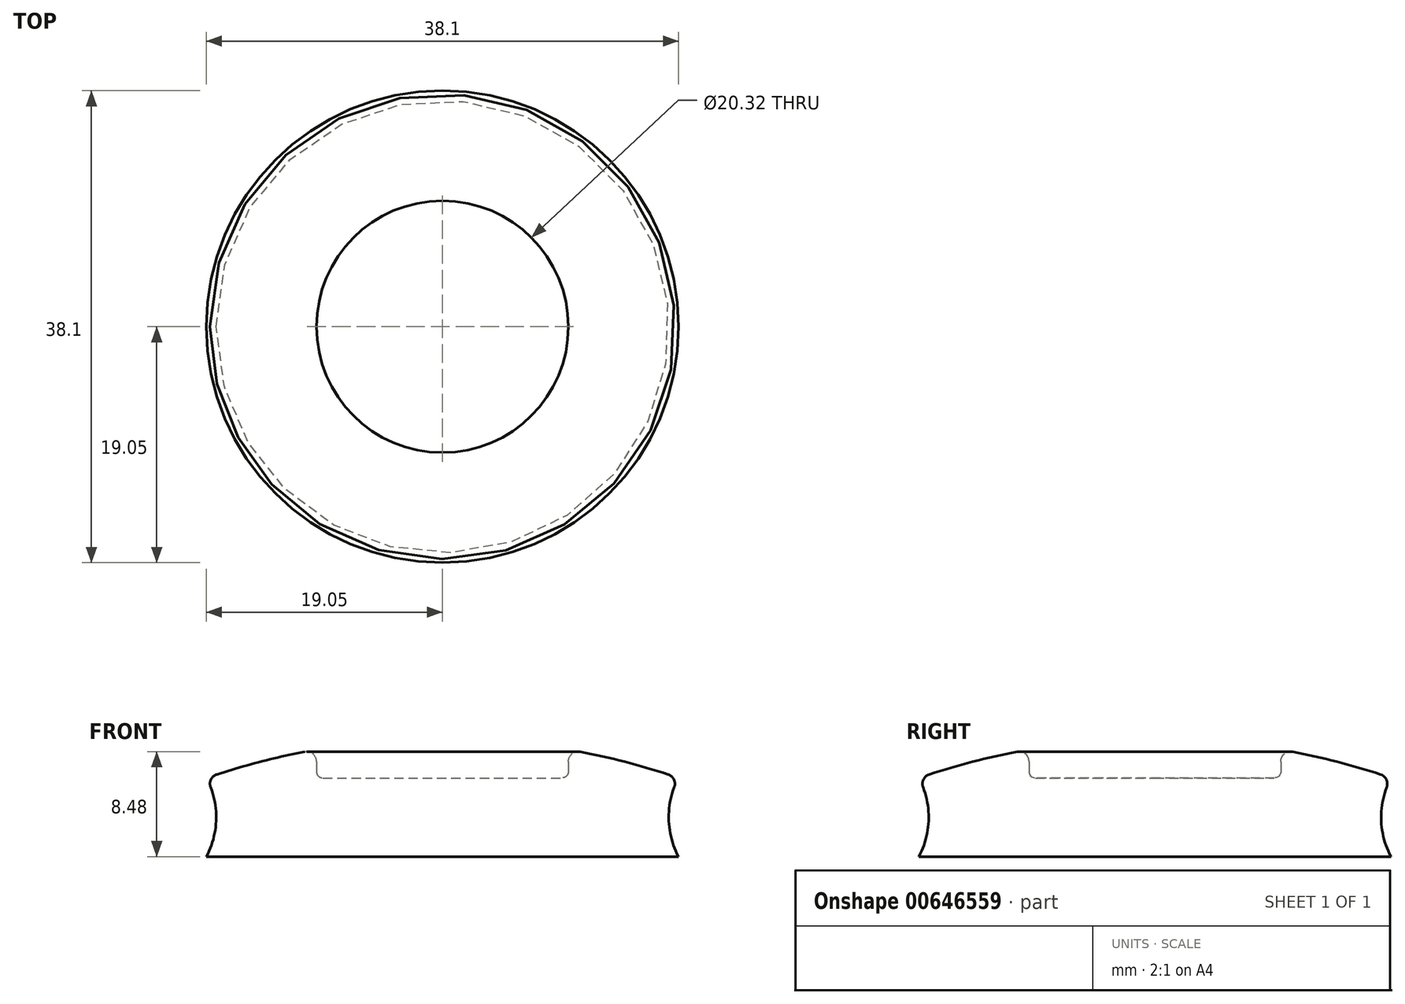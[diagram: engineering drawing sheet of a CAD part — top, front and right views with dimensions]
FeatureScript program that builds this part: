
annotation { "Feature Type Name" : "Feature", "Feature Type Description" : "" }
export const myFeature = defineFeature(function(context is Context, id is Id, definition is map)
    precondition{}
    {
        {
            var Q0;
            Q0=qCreatedBy(makeId("Front.planeOp"),FACE);
            var sketch = newSketch(context, id + "F0", { "sketchPlane" : qUnion([Q0])});
            skLineSegment(sketch, "E0.bottom", {"start": v(0, 0) * mm, "end": v(-19.05, 0) * mm});
            skLineSegment(sketch, "E0.top", {"start": v(0, 6.35) * mm, "end": v(-10.16, 6.35) * mm});
            skLineSegment(sketch, "E0.left", {"start": v(0, 0) * mm, "end": v(0, 6.35) * mm});
            skArc(sketch, "E1", {"start": v(-19.05, 0) * mm, "mid": v(-18.27, 2.76) * mm, "end": v(-18.7, 5.6) * mm});
            skLineSegment(sketch, "E2", {"start": v(0, 6.35) * mm, "end": v(19.05, 6.35) * mm});
            skLineSegment(sketch, "E3", {"start": v(0, 0) * mm, "end": v(19.05, 0) * mm});
            skArc(sketch, "E4", {"start": v(19.05, 6.35) * mm, "mid": v(14.65, 7.67) * mm, "end": v(10.16, 8.64) * mm});
            skLineSegment(sketch, "E5.bottom", {"start": v(-9.64, 6.35) * mm, "end": v(10.16, 6.35) * mm});
            skLineSegment(sketch, "E5.left", {"start": v(-10.16, 6.87) * mm, "end": v(-10.16, 7.67) * mm});
            skLineSegment(sketch, "E5.right", {"start": v(10.16, 6.35) * mm, "end": v(10.16, 8.64) * mm});
            skArc(sketch, "E6.trimOffspring", {"start": v(-11.12, 8.46) * mm, "mid": v(-14.7, 7.66) * mm, "end": v(-18.2, 6.63) * mm});
            skPoint(sketch, "E7.visualSharp", {"position": v(-19.05, 6.35) * mm});
            skArc(sketch, "E7.filletArc", {"start": v(-18.2, 6.63) * mm, "mid": v(-18.68, 6.22) * mm, "end": v(-18.7, 5.6) * mm});
            skPoint(sketch, "E8.visualSharp", {"position": v(-10.16, 8.64) * mm});
            skArc(sketch, "E8.filletArc", {"start": v(-10.16, 7.67) * mm, "mid": v(-10.45, 8.3) * mm, "end": v(-11.12, 8.46) * mm});
            skPoint(sketch, "E9.visualSharp", {"position": v(-10.16, 6.35) * mm});
            skArc(sketch, "E9.filletArc", {"start": v(-10.16, 6.87) * mm, "mid": v(-10, 6.5) * mm, "end": v(-9.64, 6.35) * mm});
            skLineSegment(sketch, "E10.trimOffspring", {"start": v(-18.6, 6.35) * mm, "end": v(-19.05, 6.35) * mm});
            skSolve(sketch);
        }
        {
            var Q0;
            Q0=makeQuery(id+"F0.imprint","IMPRINT",FACE,{"disambiguationData":[TD([[makeQuery(id+"F0.imprint","IMPRINT",EDGE,{"derivedFrom":sQuery(id+"F0.wireOp",EDGE,"E0.bottom")}),-1.0]])]});
            var Q1;
            Q1=sQuery(id+"F0.wireOp",EDGE,"E0.left");
            revolve(context, id + "F1", {"entities" : qUnion([Q0]), "axis" : qUnion([Q1]), "revolveType" : RevolveType.FULL});
        }
    });
